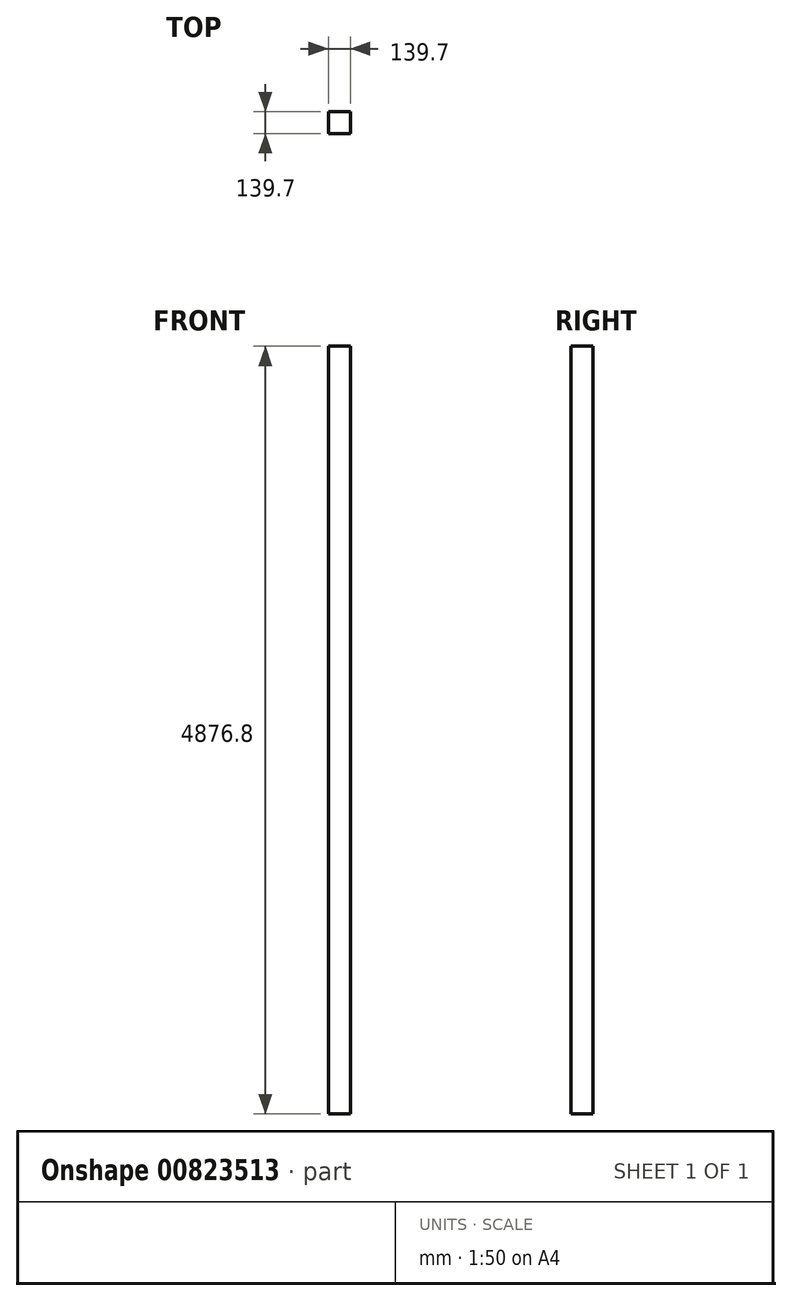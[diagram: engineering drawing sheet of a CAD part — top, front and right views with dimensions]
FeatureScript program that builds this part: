
annotation { "Feature Type Name" : "Feature", "Feature Type Description" : "" }
export const myFeature = defineFeature(function(context is Context, id is Id, definition is map)
    precondition{}
    {
        {
            var Q0;
            Q0=qCreatedBy(makeId("Top.planeOp"),FACE);
            var sketch = newSketch(context, id + "F0", { "sketchPlane" : qUnion([Q0])});
            skLineSegment(sketch, "E0.bottom", {"start": v(0, 0) * mm, "end": v(139.7, 0) * mm});
            skLineSegment(sketch, "E0.top", {"start": v(0, 139.7) * mm, "end": v(139.7, 139.7) * mm});
            skLineSegment(sketch, "E0.left", {"start": v(0, 0) * mm, "end": v(0, 139.7) * mm});
            skLineSegment(sketch, "E0.right", {"start": v(139.7, 0) * mm, "end": v(139.7, 139.7) * mm});
            skSolve(sketch);
        }
        {
            var Q0;
            Q0 = qSketchRegion(id + "F0", true);
            extrude(context, id + "F1", {"entities" : qUnion([Q0]), "depth" : 4876.8 * mm, "offsetDistance" : 25.4 * mm});
        }
    });
